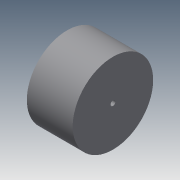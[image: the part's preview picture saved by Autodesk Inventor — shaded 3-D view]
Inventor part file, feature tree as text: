
AUTODESK INVENTOR PART (.ipt)
format: ipt  version: 2013 (Build 170138000, 138)  size: 77,312 bytes
history: native  units: mm
features: extrude x2, sketch x2
ambient origin geometry x8: Origin, YZ Plane, XZ Plane, XY Plane, X Axis, Y Axis, Z Axis, Center Point
bodies: Solid1 (feature_tree)
feature tree (4):
  extrude  "Extrusion1"  Depth=57.0mm TaperAngle=0.0deg
  extrude  "Extrusion2"  Depth=57.0mm TaperAngle=0.0deg
  sketch  "Sketch1"  dims[d0=100.0mm d1=57.0mm d2=0.0mm]
  sketch  "Sketch2"  dims[d3=6.0mm d4=57.0mm d5=0.0mm]
